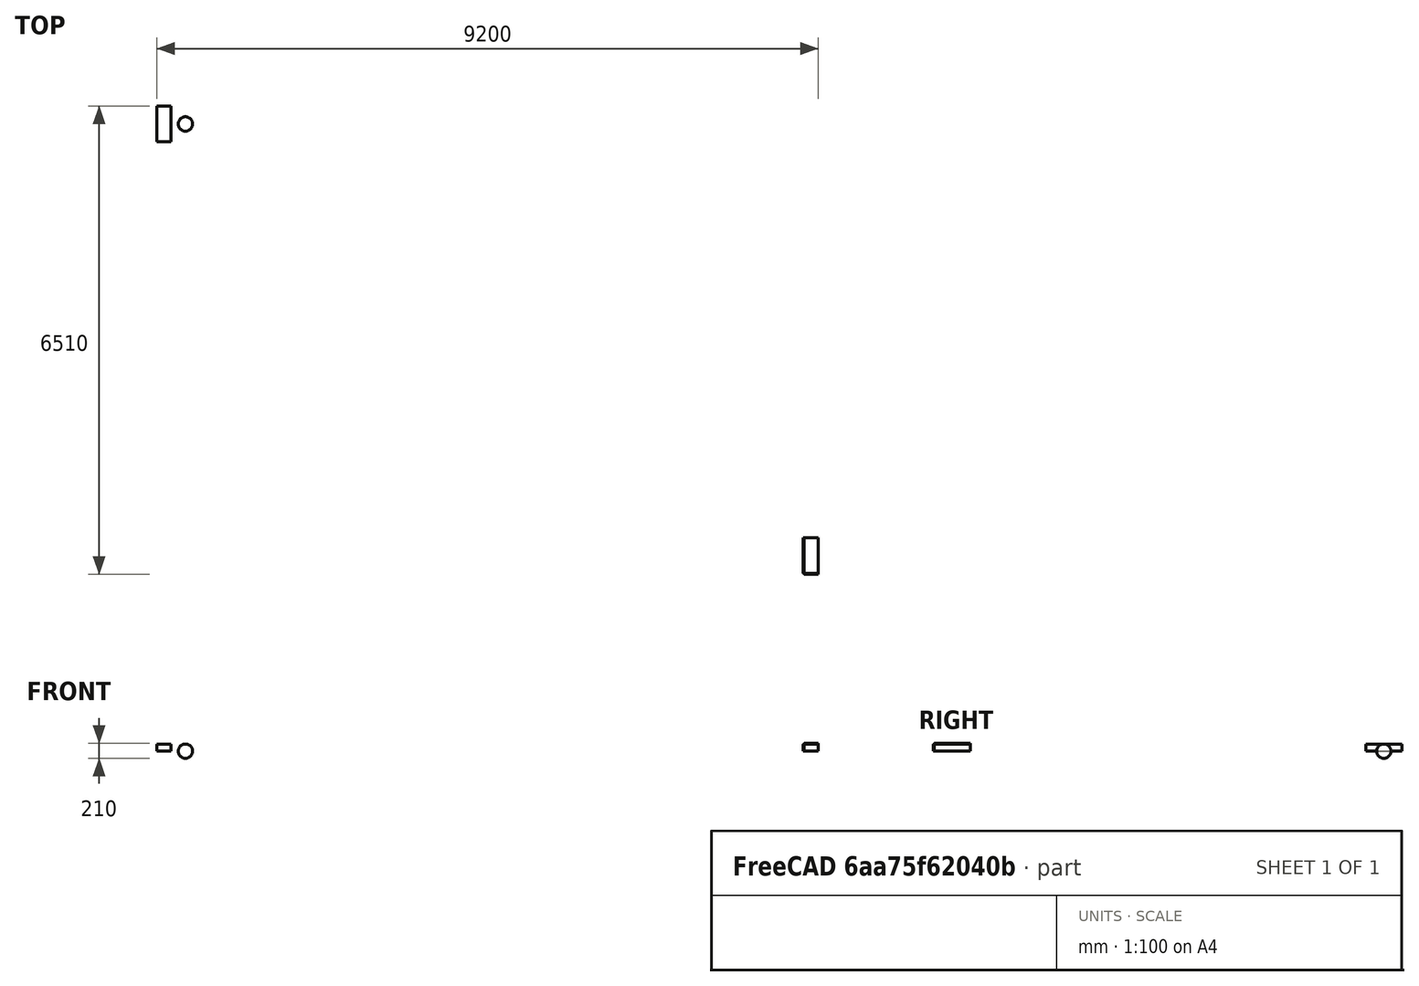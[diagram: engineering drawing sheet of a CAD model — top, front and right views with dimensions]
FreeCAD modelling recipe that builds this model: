
FCSTD DOCUMENT  (FreeCAD 1.1R14555 (Git shallow))
Label: draft_test_objects
License: All rights reserved
LicenseURL: https://en.wikipedia.org/wiki/All_rights_reserved
objects: Part::FeaturePython×40, App::Annotation×37, Part::Part2DObjectPython×20, App::FeaturePython×9, Part::Box×3, Part::Feature×1, Part::Mirroring×1, Part::Sphere×1, App::DocumentObjectGroupPython×1
note: 62 computed .brp shape members not serialized (recipe doc carries the construction recipe); baked Part::Feature solids carry a one-line shape summary decoded from their .brp

FEATURE [App::Annotation] Description
  LabelText = Draft test file | Created: 2025/08/21T22:01:30 | Version: 1.1.0 | Release: 14555 (Git shallow) https://github.com/FreeCAD/FreeCAD main | Branch: 2025/08/20 00:00:55 main 5e4fe3a3c3af46be530969d323368fee8bfcba3b
  Position = (0,-1000,0)
FEATURE [Part::Feature] Frame
  shape: bbox 18000 x 12000 x 2e-07 mm, 0 faces, 0 solids (baked)
FEATURE [Part::FeaturePython] Line  # WARN: FeaturePython — macro-defined, semantics opaque (R4)
  Area = 0
  AttacherType = Attacher::AttachEngine3D
  ChamferSize = 0
  Closed = false
  End = (500,500,0)
  FilletRadius = 0
  Length = 707.107
  MakeFace = true
  Points = (2) [(0,0,0),(500,500,0)]
  Start = (0,0,0)
  Subdivisions = 0
FEATURE [App::Annotation] Annotation
  LabelText = Line
  Position = (0,-200,0)
FEATURE [Part::FeaturePython] Wire  # WARN: FeaturePython — macro-defined, semantics opaque (R4)
  Area = 0
  AttacherType = Attacher::AttachEngine3D
  ChamferSize = 0
  Closed = false
  End = (1500,500,0)
  FilletRadius = 0
  Length = 809.017
  MakeFace = true
  Points = (3) [(1000,0,0),(1500,250,0),(1500,500,0)]
  Start = (1000,0,0)
  Subdivisions = 0
FEATURE [App::Annotation] Annotation001
  LabelText = Wire
  Position = (1000,-200,0)
FEATURE [Part::FeaturePython] Line001  # WARN: FeaturePython — macro-defined, semantics opaque (R4)
  Area = 0
  AttacherType = Attacher::AttachEngine3D
  ChamferSize = 0
  Closed = false
  End = (2000,500,0)
  FilletRadius = 0
  Length = 500
  MakeFace = true
  Points = (2) [(2000,0,0),(2000,500,0)]
  Start = (2000,0,0)
  Subdivisions = 0
FEATURE [Part::FeaturePython] Line002  # WARN: FeaturePython — macro-defined, semantics opaque (R4)
  Area = 0
  AttacherType = Attacher::AttachEngine3D
  ChamferSize = 0
  Closed = false
  End = (2500,500,0)
  FilletRadius = 0
  Length = 500
  MakeFace = true
  Points = (2) [(2000,500,0),(2500,500,0)]
  Start = (2000,500,0)
  Subdivisions = 0
FEATURE [Part::Part2DObjectPython] Fillet  # Draft 2D object (typed FeaturePython)
  End = (2500,500,0)
  FilletRadius = 400
  Length = 828.319
  Start = (2000,0,0)
FEATURE [App::Annotation] Annotation002
  LabelText = Fillet
  Position = (2000,-200,0)
FEATURE [Part::Part2DObjectPython] Arc  # Draft 2D object (typed FeaturePython)
  Area = 0
  FirstAngle = 90
  LastAngle = 270
  MakeFace = true
  Placement = pos=(3250,250,0) rot=(0,0,1;0rad)
  Radius = 250
FEATURE [App::Annotation] Annotation003
  LabelText = Circular arc
  Position = (3000,-200,0)
FEATURE [Part::Part2DObjectPython] Arc001  # Draft 2D object (typed FeaturePython)
  Area = 0
  FirstAngle = 0
  LastAngle = 180
  MakeFace = false
  Placement = pos=(4250,250,0) rot=(0.707107,-0.707107,0;3.14159rad)
  Radius = 250
FEATURE [App::Annotation] Annotation004
  LabelText = Circular arc 3 points
  Position = (4000,-200,0)
FEATURE [Part::Part2DObjectPython] Circle  # Draft 2D object (typed FeaturePython)
  Area = 196350
  FirstAngle = 0
  LastAngle = 0
  MakeFace = true
  Placement = pos=(5250,250,0) rot=(0,0,1;0rad)
  Radius = 250
FEATURE [App::Annotation] Annotation005
  LabelText = Circle
  Position = (5000,-200,0)
FEATURE [Part::Part2DObjectPython] Ellipse  # Draft 2D object (typed FeaturePython)
  Area = 117810
  FirstAngle = 0
  LastAngle = 0
  MajorRadius = 250
  MakeFace = true
  MinorRadius = 150
  Placement = pos=(6250,150,0) rot=(0,0,1;0rad)
FEATURE [App::Annotation] Annotation006
  LabelText = Ellipse
  Position = (6000,-200,0)
FEATURE [Part::Part2DObjectPython] Rectangle  # Draft 2D object (typed FeaturePython)
  Area = 150000
  ChamferSize = 0
  Columns = 1
  FilletRadius = 0
  Height = 300
  Length = 500
  MakeFace = true
  Placement = pos=(7000,0,0) rot=(0,0,1;0rad)
  Rows = 1
FEATURE [App::Annotation] Annotation007
  LabelText = Rectangle
  Position = (7000,-200,0)
FEATURE [Part::Part2DObjectPython] Polygon  # Draft 2D object (typed FeaturePython)
  Area = 148603
  ChamferSize = 0
  DrawMode = 0
  FacesNumber = 5
  FilletRadius = 0
  MakeFace = true
  Placement = pos=(8250,250,0) rot=(0,0,1;0rad)
  Radius = 250
FEATURE [App::Annotation] Annotation008
  LabelText = Polygon
  Position = (8000,-200,0)
FEATURE [Part::FeaturePython] BSpline  # WARN: FeaturePython — macro-defined, semantics opaque (R4)
  Area = 0
  AttacherType = Attacher::AttachEngine3D
  Closed = false
  MakeFace = true
  Parameterization = 1
  Points = (4) [(9000,0,0),(9100,200,0),(9400,300,0),(9500,500,0)]
FEATURE [App::Annotation] Annotation009
  LabelText = BSpline
  Position = (9000,-200,0)
FEATURE [Part::FeaturePython] BezCurve  # WARN: FeaturePython — macro-defined, semantics opaque (R4)
  Area = 0
  AttacherType = Attacher::AttachEngine3D
  Closed = false
  Degree = 3
  Length = 838.374
  MakeFace = true
  Points = (4) [(10000,0,0),(10000,500,0),(10500,0,0),(10500,500,0)]
FEATURE [App::Annotation] Annotation010
  LabelText = Cubic bezier
  Position = (10000,-200,0)
FEATURE [Part::FeaturePython] BezCurve001  # WARN: FeaturePython — macro-defined, semantics opaque (R4)
  Area = 0
  AttacherType = Attacher::AttachEngine3D
  Closed = false
  Degree = 4
  Length = 800.125
  MakeFace = true
  Points = (5) [(11000,0,0),(11100,400,0),(11250,250,0),(11400,100,0),(11500,500,0)]
FEATURE [App::Annotation] Annotation011
  LabelText = N-degree bezier
  Position = (11000,-200,0)
FEATURE [Part::FeaturePython] Point  # WARN: FeaturePython — macro-defined, semantics opaque (R4)
  Placement = pos=(12000,0,0) rot=(0,0,1;0rad)
  X = 12000
  Y = 0
  Z = 0
FEATURE [App::Annotation] Annotation012
  LabelText = Point
  Position = (12000,-200,0)
FEATURE [Part::Box] Box
  AttacherType = Attacher::AttachEngine3D
  Height = 100
  Length = 200
  Placement = pos=(13000,0,0) rot=(0,0,1;0rad)
  Width = 500
FEATURE [Part::FeaturePython] Facebinder  # WARN: FeaturePython — macro-defined, semantics opaque (R4)
  Area = 170000
  Extrusion = 10
  Faces = -> [Box]
  RemoveSplitter = false
  Sew = false
FEATURE [App::Annotation] Annotation013
  LabelText = Facebinder
  Position = (13000,-200,0)
FEATURE [Part::Part2DObjectPython] ShapeString  # Draft 2D object (typed FeaturePython)
  FontFile = ./osifont-lgpl3fe.ttf
  Fuse = false
  Justification = 6
  JustificationReference = 0
  KeepLeftMargin = false
  MakeFace = true
  ObliqueAngle = 0
  Placement = pos=(14000,0,0) rot=(0,0,1;0rad)
  ScaleToSize = true
  Size = 100
  String = Testing
  Tracking = 0
FEATURE [App::Annotation] Annotation014
  LabelText = Shapestring
  Position = (14000,-200,0)
FEATURE [Part::Part2DObjectPython] Rectangle001  # Draft 2D object (typed FeaturePython)
  Area = 150000
  ChamferSize = 0
  Columns = 1
  FilletRadius = 0
  Height = 300
  Length = 500
  MakeFace = true
  Placement = pos=(15000,0,0) rot=(0,0,1;0rad)
  Rows = 1
FEATURE [Part::FeaturePython] Hatch  # WARN: FeaturePython — macro-defined, semantics opaque (R4)
  Base = -> Rectangle001
  File = ./FCPAT.pat
  Pattern = Horizontal5
  Rotation = 45
  Scale = 10
  Translate = true
FEATURE [App::Annotation] Annotation015
  LabelText = Hatch
  Position = (15000,-200,0)
FEATURE [App::FeaturePython] Text  # WARN: FeaturePython — macro-defined, semantics opaque (R4)
  Placement = pos=(0,2100,0) rot=(0,0,1;0rad)
  Text = Testing | text
FEATURE [App::Annotation] Annotation016
  LabelText = Text
  Position = (0,1800,0)
FEATURE [App::FeaturePython] Dimension  # Draft dimension (typed FeaturePython)
  Diameter = false
  Dimline = (1000,2200,0)
  Direction = (0,0,0)
  Distance = 400
  End = (1500,2400,0)
  Normal = (0,0,1)
  Start = (1500,2000,0)
FEATURE [Part::FeaturePython] Line003  # WARN: FeaturePython — macro-defined, semantics opaque (R4)
  Area = 0
  AttacherType = Attacher::AttachEngine3D
  ChamferSize = 0
  Closed = false
  End = (1500,3000,0)
  FilletRadius = 0
  Length = 400
  MakeFace = true
  Points = (2) [(1500,2600,0),(1500,3000,0)]
  Start = (1500,2600,0)
  Subdivisions = 0
FEATURE [App::FeaturePython] Dimension001  # Draft dimension (typed FeaturePython)
  Diameter = false
  Dimline = (1000,2800,0)
  Direction = (0,0,0)
  Distance = 400
  End = (1500,3000,0)
  LinkedGeometry = -> [Line003]
  Normal = (0,0,1)
  Start = (1500,2600,0)
  Support = -> Line003
FEATURE [App::Annotation] Annotation017
  LabelText = Dimension
  Position = (1000,1800,0)
FEATURE [Part::Part2DObjectPython] Circle001  # Draft 2D object (typed FeaturePython)
  Area = 0
  FirstAngle = 0
  LastAngle = 0
  MakeFace = false
  Placement = pos=(2200,2200,0) rot=(0,0,1;0rad)
  Radius = 200
FEATURE [App::FeaturePython] Dimension002  # Draft dimension (typed FeaturePython)
  Diameter = false
  Dimline = (2300,2300,0)
  Direction = (0,0,0)
  Distance = 200
  End = (2341.42,2341.42,0)
  LinkedGeometry = -> [Circle001]
  Normal = (0,0,1)
  Start = (2200,2200,0)
  Support = -> Circle001
FEATURE [Part::Part2DObjectPython] Circle002  # Draft 2D object (typed FeaturePython)
  Area = 0
  FirstAngle = 0
  LastAngle = 0
  MakeFace = false
  Placement = pos=(2200,2800,0) rot=(0,0,1;0rad)
  Radius = 200
FEATURE [App::FeaturePython] Dimension003  # Draft dimension (typed FeaturePython)
  Diameter = true
  Dimline = (2300,2900,0)
  Direction = (0,0,0)
  Distance = 400
  End = (2341.42,2941.42,0)
  LinkedGeometry = -> [Circle002]
  Normal = (0,0,1)
  Start = (2058.58,2658.58,0)
  Support = -> Circle002
FEATURE [App::Annotation] Annotation018
  LabelText = Radius dimension | Diameter dimension
  Position = (2000,1800,0)
FEATURE [Part::FeaturePython] Line004  # WARN: FeaturePython — macro-defined, semantics opaque (R4)
  Area = 0
  AttacherType = Attacher::AttachEngine3D
  ChamferSize = 0
  Closed = false
  End = (3500,2000,0)
  FilletRadius = 0
  Length = 500
  MakeFace = true
  Points = (2) [(3000,2000,0),(3500,2000,0)]
  Start = (3000,2000,0)
  Subdivisions = 0
FEATURE [Part::FeaturePython] Line005  # WARN: FeaturePython — macro-defined, semantics opaque (R4)
  Area = 0
  AttacherType = Attacher::AttachEngine3D
  ChamferSize = 0
  Closed = false
  End = (3500,2500,0)
  FilletRadius = 0
  Length = 707.107
  MakeFace = true
  Points = (2) [(3000,2000,0),(3500,2500,0)]
  Start = (3000,2000,0)
  Subdivisions = 0
FEATURE [App::FeaturePython] Dimension004  # Draft dimension (typed FeaturePython)
  Angle = 45
  Center = (3000,2000,0)
  Dimline = (3250,2250,0)
  FirstAngle = 0
  LastAngle = 45
  Normal = (0,0,1)
FEATURE [App::Annotation] Annotation019
  LabelText = Angle dimension
  Position = (3000,1800,0)
FEATURE [App::FeaturePython] dLabel  # WARN: FeaturePython — macro-defined, semantics opaque (R4)
  CustomText = Example label
  LabelType = 0
  Placement = pos=(4250,2250,0) rot=(0,0,1;0rad)
  Points = (3) [(4250,2250,0),(4150,2250,0),(4000,2000,0)]
  StraightDirection = 0
  StraightDistance = -100
  TargetPoint = (4000,2000,0)
  Text = Example label
FEATURE [App::Annotation] Annotation020
  LabelText = Label
  Position = (4000,1800,0)
FEATURE [Part::Part2DObjectPython] Rectangle002  # Draft 2D object (typed FeaturePython)
  Area = 5000
  ChamferSize = 0
  Columns = 1
  FilletRadius = 0
  Height = 50
  Length = 100
  MakeFace = true
  Placement = pos=(0,4000,0) rot=(0,0,1;0rad)
  Rows = 1
FEATURE [Part::FeaturePython] Array  # Draft array (typed FeaturePython)
  Angle = 360
  ArrayType = 0
  Axis = (0,0,1)
  Base = -> Rectangle002
  Center = (0,0,0)
  Count = 6
  Fuse = false
  IntervalAxis = (0,0,0)
  IntervalX = (200,0,0)
  IntervalY = (0,150,0)
  IntervalZ = (0,0,0)
  NumberCircles = 3
  NumberPolar = 5
  NumberX = 3
  NumberY = 2
  NumberZ = 1
  PlacementList = 6 placements: [(0,4000,0),(0,4150,0),(200,4000,0),(200,4150,0),(400,4000,0),(400,4150,0)]
  RadialDistance = 50
  Symmetry = 1
  TangentialDistance = 25
FEATURE [App::Annotation] Annotation021
  LabelText = Orthogonal array
  Position = (0,3800,0)
FEATURE [Part::Part2DObjectPython] Rectangle003  # Draft 2D object (typed FeaturePython)
  Area = 2500
  ChamferSize = 0
  Columns = 1
  FilletRadius = 0
  Height = 50
  Length = 50
  MakeFace = true
  Placement = pos=(1000,4000,0) rot=(0,0,1;0rad)
  Rows = 1
FEATURE [Part::FeaturePython] Array001  # Draft array (typed FeaturePython)
  AlwaysSyncPlacement = false
  Angle = 360
  ArrayType = 0
  Axis = (0,0,1)
  Base = -> Rectangle003
  Center = (0,0,0)
  Count = 6
  ExpandArray = false
  Fuse = false
  IntervalAxis = (0,0,0)
  IntervalX = (200,0,0)
  IntervalY = (0,150,0)
  IntervalZ = (0,0,0)
  NumberCircles = 3
  NumberPolar = 5
  NumberX = 3
  NumberY = 2
  NumberZ = 1
  PlacementList = 6 placements: [(1000,4000,0),(1000,4150,0),(1200,4000,0),(1200,4150,0),(1400,4000,0),(1400,4150,0)]
  RadialDistance = 50
  ScaleList = (6) [(1,1,1),(1,1,1),(1,1,1),(1,1,1),(1,1,1),(1,1,1)]
  Symmetry = 1
  TangentialDistance = 25
FEATURE [App::Annotation] Annotation022
  LabelText = Orthogonal link array
  Position = (1000,3800,0)
FEATURE [Part::FeaturePython] Wire001  # WARN: FeaturePython — macro-defined, semantics opaque (R4)
  Area = 0
  AttacherType = Attacher::AttachEngine3D
  ChamferSize = 0
  Closed = false
  End = (2100,4000,0)
  FilletRadius = 0
  Length = 150
  MakeFace = true
  Points = (3) [(2000,4050,0),(2000,4000,0),(2100,4000,0)]
  Start = (2000,4050,0)
  Subdivisions = 0
FEATURE [Part::FeaturePython] Array002  # Draft array (typed FeaturePython)
  Angle = 90
  ArrayType = 1
  Axis = (0,0,1)
  Base = -> Wire001
  Center = (2000,4250,0)
  Count = 4
  Fuse = false
  IntervalAxis = (0,0,0)
  IntervalX = (50,0,0)
  IntervalY = (0,50,0)
  IntervalZ = (0,0,50)
  NumberCircles = 3
  NumberPolar = 4
  NumberX = 2
  NumberY = 2
  NumberZ = 1
  PlacementList = 4 placements: [(0,0,0),(2392.95,-430.608,0),(4680.61,392.949,0),(6250,2250,0)]
  RadialDistance = 50
  Symmetry = 1
  TangentialDistance = 25
FEATURE [App::Annotation] Annotation023
  LabelText = Polar array
  Position = (2000,3800,0)
FEATURE [Part::FeaturePython] Wire002  # WARN: FeaturePython — macro-defined, semantics opaque (R4)
  Area = 0
  AttacherType = Attacher::AttachEngine3D
  ChamferSize = 0
  Closed = false
  End = (3050,4000,0)
  FilletRadius = 0
  Length = 100
  MakeFace = true
  Points = (3) [(3000,4050,0),(3000,4000,0),(3050,4000,0)]
  Start = (3000,4050,0)
  Subdivisions = 0
FEATURE [Part::FeaturePython] Array003  # Draft array (typed FeaturePython)
  AlwaysSyncPlacement = false
  Angle = 90
  ArrayType = 1
  Axis = (0,0,1)
  Base = -> Wire002
  Center = (3000,4250,0)
  Count = 4
  ExpandArray = false
  Fuse = false
  IntervalAxis = (0,0,0)
  IntervalX = (50,0,0)
  IntervalY = (0,50,0)
  IntervalZ = (0,0,50)
  NumberCircles = 3
  NumberPolar = 4
  NumberX = 2
  NumberY = 2
  NumberZ = 1
  PlacementList = 4 placements: [(0,0,0),(2526.92,-930.608,0),(5180.61,-473.076,0),(7250,1250,0)]
  RadialDistance = 50
  ScaleList = (4) [(1,1,1),(1,1,1),(1,1,1),(1,1,1)]
  Symmetry = 1
  TangentialDistance = 25
FEATURE [App::Annotation] Annotation024
  LabelText = Polar link array
  Position = (3000,3800,0)
FEATURE [Part::Part2DObjectPython] Polygon001  # Draft 2D object (typed FeaturePython)
  Area = 1169.13
  ChamferSize = 0
  DrawMode = 0
  FacesNumber = 3
  FilletRadius = 0
  MakeFace = true
  Placement = pos=(4250,4250,0) rot=(0,0,1;0rad)
  Radius = 30
FEATURE [Part::FeaturePython] Array004  # Draft array (typed FeaturePython)
  Angle = 360
  ArrayType = 2
  Axis = (0,0,1)
  Base = -> Polygon001
  Center = (4250,4250,0)
  Count = 20
  Fuse = false
  IntervalAxis = (0,0,0)
  IntervalX = (50,0,0)
  IntervalY = (0,50,0)
  IntervalZ = (0,0,50)
  NumberCircles = 3
  NumberPolar = 5
  NumberX = 2
  NumberY = 2
  NumberZ = 1
  PlacementList = 20 placements: [(4250,4250,0),(4140,4250,0),(4195,4154.74,0),(4305,4154.74,0),(4360,4250,0),(4305,4345.26,0),(4195,4345.26,0),(4030,4250,0),(4055.2,4147.76,0),(4125.03,4068.94,0),(4223.48,4031.6,0),(4328.01,4044.3,0),(4414.67,4104.11,0),(4463.61,4197.35,0),(4463.61,4302.65,0),(4414.67,4395.89,0),(4328.01,4455.7,0),(4223.48,4468.4,0),(4125.03,4431.06,0),(4055.2,4352.24,0)]
  RadialDistance = 110
  Symmetry = 1
  TangentialDistance = 100
FEATURE [App::Annotation] Annotation025
  LabelText = Circular array
  Position = (4000,3800,0)
FEATURE [Part::Part2DObjectPython] Polygon002  # Draft 2D object (typed FeaturePython)
  Area = 1800
  ChamferSize = 0
  DrawMode = 0
  FacesNumber = 4
  FilletRadius = 0
  MakeFace = true
  Placement = pos=(5250,4250,0) rot=(0,0,1;0rad)
  Radius = 30
FEATURE [Part::FeaturePython] Array005  # Draft array (typed FeaturePython)
  AlwaysSyncPlacement = false
  Angle = 360
  ArrayType = 2
  Axis = (0,0,1)
  Base = -> Polygon002
  Center = (5250,4250,0)
  Count = 20
  ExpandArray = false
  Fuse = false
  IntervalAxis = (0,0,0)
  IntervalX = (50,0,0)
  IntervalY = (0,50,0)
  IntervalZ = (0,0,50)
  NumberCircles = 3
  NumberPolar = 5
  NumberX = 2
  NumberY = 2
  NumberZ = 1
  PlacementList = 20 placements: [(5250,4250,0),(5140,4250,0),(5195,4154.74,0),(5305,4154.74,0),(5360,4250,0),(5305,4345.26,0),(5195,4345.26,0),(5030,4250,0),(5055.2,4147.76,0),(5125.03,4068.94,0),(5223.48,4031.6,0),(5328.01,4044.3,0),(5414.67,4104.11,0),(5463.61,4197.35,0),(5463.61,4302.65,0),(5414.67,4395.89,0),(5328.01,4455.7,0),(5223.48,4468.4,0),(5125.03,4431.06,0),(5055.2,4352.24,0)]
  RadialDistance = 110
  ScaleList = (20) [(1,1,1),(1,1,1),(1,1,1),(1,1,1),(1,1,1),(1,1,1),(1,1,1),(1,1,1),(1,1,1),(1,1,1),(1,1,1),(1,1,1),(1,1,1),(1,1,1),(1,1,1),(1,1,1),(1,1,1),(1,1,1),(1,1,1),(1,1,1)]
  Symmetry = 1
  TangentialDistance = 100
FEATURE [App::Annotation] Annotation026
  LabelText = Circular link array
  Position = (5000,3800,0)
FEATURE [Part::Part2DObjectPython] Polygon003  # Draft 2D object (typed FeaturePython)
  Area = 1169.13
  ChamferSize = 0
  DrawMode = 0
  FacesNumber = 3
  FilletRadius = 0
  MakeFace = true
  Placement = pos=(6000,4000,0) rot=(0,0,1;0rad)
  Radius = 30
FEATURE [Part::FeaturePython] BSpline001  # WARN: FeaturePython — macro-defined, semantics opaque (R4)
  Area = 0
  AttacherType = Attacher::AttachEngine3D
  Closed = false
  MakeFace = true
  Parameterization = 1
  Points = (4) [(6000,4000,0),(6100,4200,0),(6400,4300,0),(6500,4500,0)]
FEATURE [Part::FeaturePython] PathArray  # WARN: FeaturePython — macro-defined, semantics opaque (R4)
  Align = false
  AlignMode = 0
  Base = -> Polygon003
  Count = 5
  EndOffset = 0
  ExtraTranslation = (0,0,0)
  ForceVertical = false
  Fuse = false
  PathObject = -> BSpline001
  PlacementList = 5 placements: [(6000,4000,0),(6067.31,4178.13,0),(6250,4250,0),(6432.69,4321.87,0),(6500,4500,0)]
  ReversePath = false
  SpacingMode = 0
  SpacingPattern = [1,2]
  SpacingUnit = 20
  StartOffset = 0
  TangentVector = (1,0,0)
  UseSpacingPattern = false
  VerticalVector = (0,0,1)
FEATURE [App::Annotation] Annotation027
  LabelText = Path array
  Position = (6000,3800,0)
FEATURE [Part::Part2DObjectPython] Polygon004  # Draft 2D object (typed FeaturePython)
  Area = 1800
  ChamferSize = 0
  DrawMode = 0
  FacesNumber = 4
  FilletRadius = 0
  MakeFace = true
  Placement = pos=(7000,4000,0) rot=(0,0,1;0rad)
  Radius = 30
FEATURE [Part::FeaturePython] BSpline002  # WARN: FeaturePython — macro-defined, semantics opaque (R4)
  Area = 0
  AttacherType = Attacher::AttachEngine3D
  Closed = false
  MakeFace = true
  Parameterization = 1
  Points = (4) [(7000,4000,0),(7100,4200,0),(7400,4300,0),(7500,4500,0)]
FEATURE [Part::FeaturePython] PathArray001  # WARN: FeaturePython — macro-defined, semantics opaque (R4)
  Align = false
  AlignMode = 0
  AlwaysSyncPlacement = false
  Base = -> Polygon004
  Count = 5
  EndOffset = 0
  ExpandArray = false
  ExtraTranslation = (0,0,0)
  ForceVertical = false
  Fuse = false
  PathObject = -> BSpline002
  PlacementList = 5 placements: [(7000,4000,0),(7067.31,4178.13,0),(7250,4250,0),(7432.69,4321.87,0),(7500,4500,0)]
  ReversePath = false
  ScaleList = (5) [(1,1,1),(1,1,1),(1,1,1),(1,1,1),(1,1,1)]
  SpacingMode = 0
  SpacingPattern = [1,2]
  SpacingUnit = 20
  StartOffset = 0
  TangentVector = (1,0,0)
  UseSpacingPattern = false
  VerticalVector = (0,0,1)
FEATURE [App::Annotation] Annotation028
  LabelText = Path link array
  Position = (7000,3800,0)
FEATURE [Part::Part2DObjectPython] Polygon005  # Draft 2D object (typed FeaturePython)
  Area = 1169.13
  ChamferSize = 0
  DrawMode = 0
  FacesNumber = 3
  FilletRadius = 0
  MakeFace = true
  Placement = pos=(8000,4000,0) rot=(0,0,1;0rad)
  Radius = 30
FEATURE [Part::FeaturePython] Point001  # WARN: FeaturePython — macro-defined, semantics opaque (R4)
  Placement = pos=(8030,4030,0) rot=(0,0,1;0rad)
  X = 8030
  Y = 4030
  Z = 0
FEATURE [Part::FeaturePython] Point002  # WARN: FeaturePython — macro-defined, semantics opaque (R4)
  Placement = pos=(8030,4250,0) rot=(0,0,1;0rad)
  X = 8030
  Y = 4250
  Z = 0
FEATURE [Part::FeaturePython] Point003  # WARN: FeaturePython — macro-defined, semantics opaque (R4)
  Placement = pos=(8470,4250,0) rot=(0,0,1;0rad)
  X = 8470
  Y = 4250
  Z = 0
FEATURE [Part::FeaturePython] Point004  # WARN: FeaturePython — macro-defined, semantics opaque (R4)
  Placement = pos=(8470,4470,0) rot=(0,0,1;0rad)
  X = 8470
  Y = 4470
  Z = 0
FEATURE [Part::FeaturePython] Block  # WARN: FeaturePython — macro-defined, semantics opaque (R4)
  AttacherType = Attacher::AttachEngine3D
  Components = -> [Point001,Point002,Point003,Point004]
FEATURE [Part::FeaturePython] PointArray  # Draft array (typed FeaturePython)
  Base = -> Polygon005
  Count = 4
  Fuse = false
  PlacementList = 4 placements: [(8030,4030,0),(8030,4250,0),(8470,4250,0),(8470,4470,0)]
  PointObject = -> Block
FEATURE [App::Annotation] Annotation029
  LabelText = Point array
  Position = (8000,3800,0)
FEATURE [Part::Part2DObjectPython] Polygon006  # Draft 2D object (typed FeaturePython)
  Area = 1800
  ChamferSize = 0
  DrawMode = 0
  FacesNumber = 4
  FilletRadius = 0
  MakeFace = true
  Placement = pos=(9000,4000,0) rot=(0,0,1;0rad)
  Radius = 30
FEATURE [Part::FeaturePython] Point005  # WARN: FeaturePython — macro-defined, semantics opaque (R4)
  Placement = pos=(9030,4030,0) rot=(0,0,1;0rad)
  X = 9030
  Y = 4030
  Z = 0
FEATURE [Part::FeaturePython] Point006  # WARN: FeaturePython — macro-defined, semantics opaque (R4)
  Placement = pos=(9030,4250,0) rot=(0,0,1;0rad)
  X = 9030
  Y = 4250
  Z = 0
FEATURE [Part::FeaturePython] Point007  # WARN: FeaturePython — macro-defined, semantics opaque (R4)
  Placement = pos=(9470,4250,0) rot=(0,0,1;0rad)
  X = 9470
  Y = 4250
  Z = 0
FEATURE [Part::FeaturePython] Point008  # WARN: FeaturePython — macro-defined, semantics opaque (R4)
  Placement = pos=(9470,4470,0) rot=(0,0,1;0rad)
  X = 9470
  Y = 4470
  Z = 0
FEATURE [Part::FeaturePython] Block001  # WARN: FeaturePython — macro-defined, semantics opaque (R4)
  AttacherType = Attacher::AttachEngine3D
  Components = -> [Point005,Point006,Point007,Point008]
FEATURE [Part::FeaturePython] PointArray001  # Draft array (typed FeaturePython)
  AlwaysSyncPlacement = false
  Base = -> Polygon006
  Count = 4
  ExpandArray = false
  Fuse = false
  PlacementList = 4 placements: [(9030,4030,0),(9030,4250,0),(9470,4250,0),(9470,4470,0)]
  PointObject = -> Block001
  ScaleList = (4) [(1,1,1),(1,1,1),(1,1,1),(1,1,1)]
FEATURE [App::Annotation] Annotation030
  LabelText = Point link array
  Position = (9000,3800,0)
FEATURE [Part::FeaturePython] Wire003  # WARN: FeaturePython — macro-defined, semantics opaque (R4)
  Area = 0
  AttacherType = Attacher::AttachEngine3D
  ChamferSize = 0
  Closed = false
  End = (500,6000,0)
  FilletRadius = 0
  Length = 653.113
  MakeFace = true
  Points = (3) [(0,6000,0),(150,6200,0),(500,6000,0)]
  Start = (0,6000,0)
  Subdivisions = 0
FEATURE [Part::Mirroring] Mirror  label="Wire003 (gespiegeld)"
  Base = (0,6250,0)
  Normal = (0,-1,0)
  Source = -> Wire003
FEATURE [App::Annotation] Annotation031
  LabelText = Mirror
  Position = (0,5800,0)
FEATURE [Part::FeaturePython] Wire004  # WARN: FeaturePython — macro-defined, semantics opaque (R4)
  Area = 0
  AttacherType = Attacher::AttachEngine3D
  ChamferSize = 0
  Closed = false
  End = (1500,6000,0)
  FilletRadius = 0
  Length = 653.113
  MakeFace = true
  Points = (3) [(1000,6000,0),(1150,6200,0),(1500,6000,0)]
  Start = (1000,6000,0)
  Subdivisions = 0
FEATURE [Part::FeaturePython] Clone  label="Wire005"  # Draft clone (typed FeaturePython)
  AttacherType = Attacher::AttachEngine3D
  ForceCompound = false
  Fuse = false
  Objects = -> [Wire004]
  Placement = pos=(0,300,0) rot=(0,0,1;0rad)
  Scale = (1,1,1)
FEATURE [App::Annotation] Annotation032
  LabelText = Clone
  Position = (1000,5800,0)
FEATURE [Part::Box] Box001
  AttacherType = Attacher::AttachEngine3D
  Height = 100
  Length = 200
  Placement = pos=(2000,6000,0) rot=(-0.534522,0.267261,0;0.640522rad)
  Width = 500
FEATURE [Part::Part2DObjectPython] Shape2DView  # Draft 2D object (typed FeaturePython)
  AutoUpdate = true
  Base = -> Box001
  Clip = false
  FuseArch = false
  HiddenLines = false
  InPlace = true
  OnlySolids = false
  Projection = (0,0,1)
  ProjectionMode = 0
  SegmentLength = 0.05
  Tessellation = false
  VisibleOnly = false
FEATURE [App::Annotation] Annotation033
  LabelText = Shape2DView
  Position = (2000,5800,0)
FEATURE [App::FeaturePython] WPProxy  # WARN: FeaturePython — macro-defined, semantics opaque (R4)
  Placement = pos=(3250,6250,0) rot=(0,0,1;0rad)
FEATURE [App::Annotation] Annotation034
  LabelText = WorkingPlaneProxy
  Position = (3000,5800,0)
FEATURE [Part::Box] Box002
  AttacherType = Attacher::AttachEngine3D
  Height = 100
  Length = 200
  Placement = pos=(4000,6000,0) rot=(0,0,1;0rad)
  Width = 500
FEATURE [Part::Sphere] Sphere
  Angle1 = -90
  Angle2 = 90
  Angle3 = 360
  AttacherType = Attacher::AttachEngine3D
  Placement = pos=(4400,6250,0) rot=(0,0,1;0rad)
  Radius = 100
FEATURE [App::FeaturePython] Layer  label="Custom layer"  # WARN: FeaturePython — macro-defined, semantics opaque (R4)
  Group = -> [Box002,Sphere]
FEATURE [App::DocumentObjectGroupPython] LayerContainer  label="Lagen"  # scripted group (container) (typed FeaturePython)
  Group = -> [Layer]
FEATURE [App::Annotation] Annotation035
  LabelText = Layer
  Position = (4000,5800,0)
